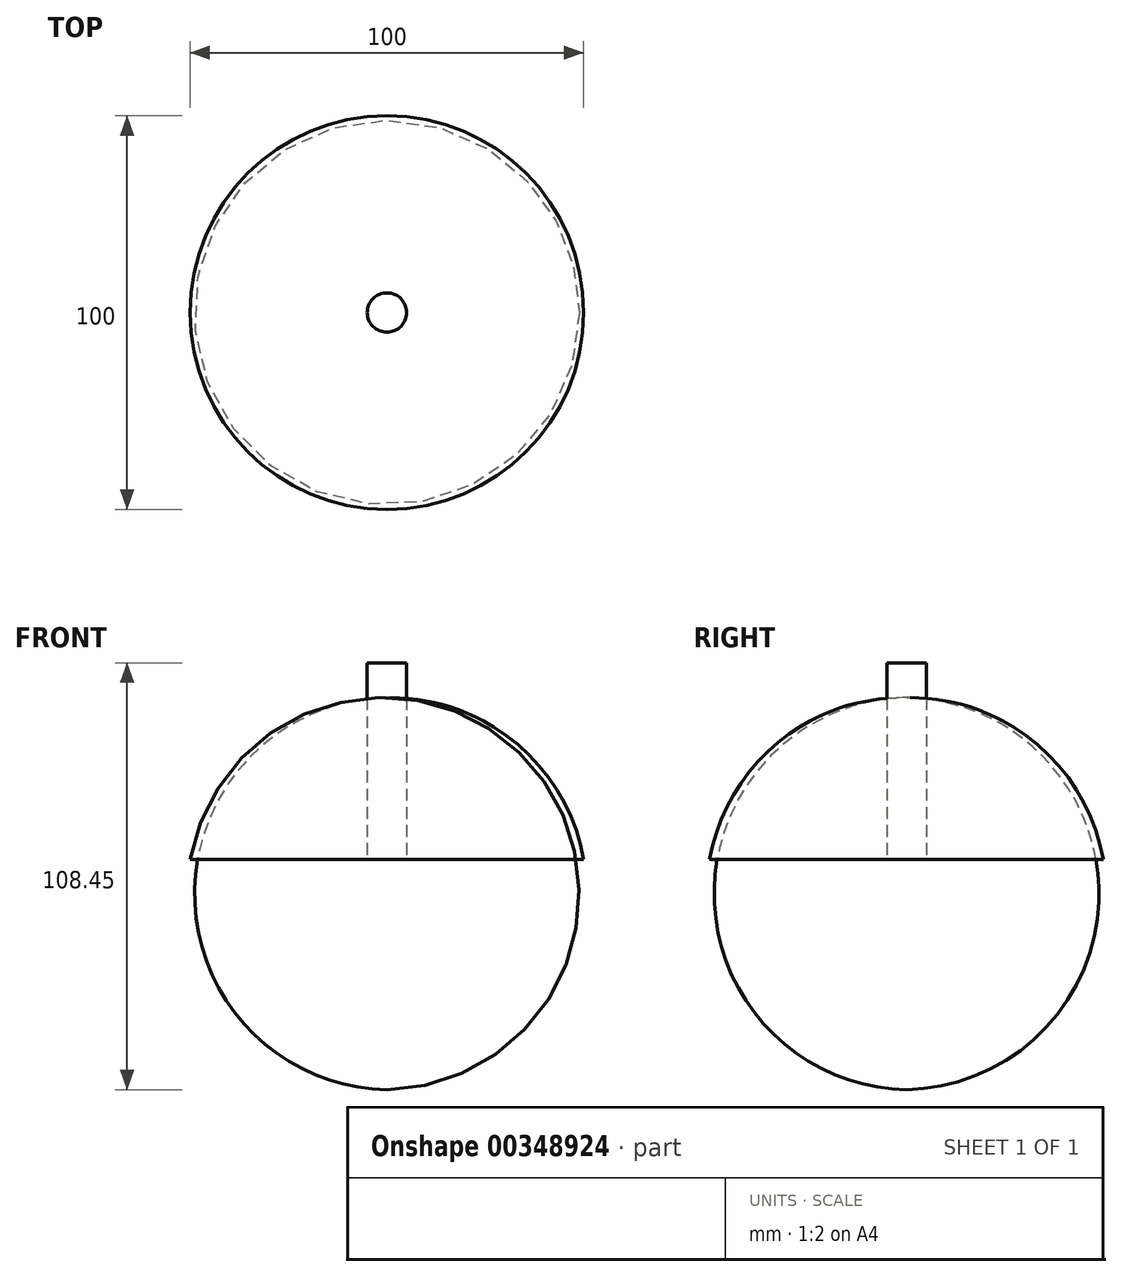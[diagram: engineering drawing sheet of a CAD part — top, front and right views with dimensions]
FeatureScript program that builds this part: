
annotation { "Feature Type Name" : "Feature", "Feature Type Description" : "" }
export const myFeature = defineFeature(function(context is Context, id is Id, definition is map)
    precondition{}
    {
        {
            var Q0;
            Q0=qCreatedBy(makeId("Front.planeOp"),FACE);
            var sketch = newSketch(context, id + "F0", { "sketchPlane" : qUnion([Q0])});
            skLineSegment(sketch, "E0.bottom", {"start": v(0, 0) * mm, "end": v(50, 0) * mm});
            skLineSegment(sketch, "E0.left", {"start": v(0, 0) * mm, "end": v(0, 41.15) * mm});
            skArc(sketch, "E1", {"start": v(50, 0) * mm, "mid": v(32.6, 29.8) * mm, "end": v(0, 41.15) * mm});
            skPoint(sketch, "E2.middle", {"position": v(16.59, 14.67) * mm});
            skLineSegment(sketch, "E3", {"start": v(19.13, 14.3) * mm, "end": v(19.4, 14.66) * mm, "construction": true});
            skLineSegment(sketch, "E4", {"start": v(16.59, 12.1) * mm, "end": v(16.62, 12.08) * mm, "construction": true});
            skFitSpline(sketch, "E5", {"points": [v(16.51, 16.92) * mm, v(20.39, 20.55) * mm, v(24.88, 22) * mm, v(22.66, 17.82) * mm], "startDerivative": vector(9.16, 11.04) * mm, "endDerivative": vector(-23.26, -14.59) * mm});
            skFitSpline(sketch, "E6", {"points": [v(22.66, 17.82) * mm, v(19.4, 14.66) * mm, v(18.83, 14.43) * mm, v(18.83, 14.4) * mm], "startDerivative": vector(-3.06, -8.88) * mm, "endDerivative": vector(0.1, -0.53) * mm});
            skFitSpline(sketch, "E7", {"points": [v(18.83, 14.4) * mm, v(21.75, 12.97) * mm, v(23.56, 10.14) * mm, v(24.88, 8.11) * mm], "startDerivative": vector(9.23, -3) * mm, "endDerivative": vector(4.43, -6.23) * mm});
            skFitSpline(sketch, "E8", {"points": [v(24.88, 8.11) * mm, v(25.94, 7.28) * mm, v(26.09, 7) * mm, v(25.28, 6.88) * mm, v(23.87, 7.33) * mm], "startDerivative": vector(4.07, -3.09) * mm, "endDerivative": vector(-4.32, 2) * mm});
            skFitSpline(sketch, "E9", {"points": [v(16.62, 12.08) * mm, v(18.93, 9.84) * mm, v(23.87, 7.33) * mm], "startDerivative": vector(4.6, -5.37) * mm, "endDerivative": vector(9.67, -4.2) * mm});
            skLineSegment(sketch, "E10.trimOffspring", {"start": v(18.83, 14.4) * mm, "end": v(18.83, 14.4) * mm});
            skPoint(sketch, "E11.orphan", {"position": v(24.88, 7.33) * mm});
            skFitSpline(sketch, "E12.MirrorCS", {"points": [v(16.66, 16.92) * mm, v(12.78, 20.55) * mm, v(8.3, 22) * mm, v(10.52, 17.82) * mm], "startDerivative": vector(-9.16, 11.04) * mm, "endDerivative": vector(23.26, -14.59) * mm});
            skFitSpline(sketch, "E13.MirrorCS", {"points": [v(10.52, 17.82) * mm, v(13.77, 14.66) * mm, v(14.34, 14.43) * mm, v(14.34, 14.4) * mm], "startDerivative": vector(3.06, -8.88) * mm, "endDerivative": vector(-0.1, -0.53) * mm});
            skFitSpline(sketch, "E14.MirrorCS", {"points": [v(14.34, 14.4) * mm, v(11.42, 12.97) * mm, v(9.61, 10.14) * mm, v(8.3, 8.11) * mm], "startDerivative": vector(-9.23, -3) * mm, "endDerivative": vector(-4.43, -6.23) * mm});
            skFitSpline(sketch, "E15.MirrorCS", {"points": [v(16.55, 12.08) * mm, v(14.25, 9.84) * mm, v(9.3, 7.33) * mm], "startDerivative": vector(-4.6, -5.37) * mm, "endDerivative": vector(-9.67, -4.2) * mm});
            skFitSpline(sketch, "E16.MirrorCS", {"points": [v(8.3, 8.11) * mm, v(7.23, 7.28) * mm, v(7.1, 7.06) * mm, v(7.9, 6.88) * mm, v(9.3, 7.33) * mm], "startDerivative": vector(-4.07, -3.09) * mm, "endDerivative": vector(4.32, 2) * mm});
            skPoint(sketch, "E17.orphan", {"position": v(16.59, 22) * mm});
            skPoint(sketch, "E18.orphan", {"position": v(8.3, 7.33) * mm});
            skLineSegment(sketch, "E19.trimOffspring", {"start": v(16.59, 7.33) * mm, "end": v(16.59, 7.01) * mm, "construction": true});
            skEllipse(sketch, "E20", {"center": v(32.68, 12.4) * mm, "majorRadius": 2.06 * mm, "minorRadius": 0.68 * mm, "majorAxis": v(0.9, -0.43)});
            skFitSpline(sketch, "E21", {"points": [v(6.55, 37.72) * mm, v(6.85, 34.97) * mm, v(10.86, 33.56) * mm, v(12.41, 32.82) * mm, v(11.08, 35.57) * mm, v(8.48, 36.46) * mm, v(6.55, 37.72) * mm]});
            skFitSpline(sketch, "E22", {"points": [v(20.8, 27.7) * mm, v(21.47, 30) * mm, v(25.25, 31.4) * mm, v(25.85, 33.34) * mm, v(26.89, 29.33) * mm, v(23.92, 27.85) * mm, v(22.21, 26.07) * mm, v(20.8, 26.14) * mm, v(20.8, 27.7) * mm]});
            skFitSpline(sketch, "E23", {"points": [v(34.53, 8.55) * mm, v(34.75, 6.03) * mm, v(37.35, 5.43) * mm, v(38.4, 2.98) * mm, v(39.2, 5.58) * mm, v(38.84, 7.14) * mm, v(37.28, 7.51) * mm, v(35.42, 11.15) * mm, v(34.53, 8.55) * mm]});
            skFitSpline(sketch, "E24", {"points": [v(29.56, 20.5) * mm, v(31.2, 22.73) * mm, v(34.53, 23.91) * mm, v(34.6, 25.1) * mm, v(36.02, 21.9) * mm, v(34.46, 19.76) * mm, v(31.79, 18.72) * mm, v(28.97, 15.45) * mm, v(29.26, 19.68) * mm, v(29.56, 20.5) * mm]});
            skFitSpline(sketch, "E25", {"points": [v(4.7, 16.34) * mm, v(2.4, 15.3) * mm, v(1.73, 12.78) * mm, v(2.62, 9.59) * mm, v(3.43, 11) * mm, v(4.47, 13.15) * mm, v(6.77, 13.6) * mm, v(7.37, 15.45) * mm, v(8.3, 16.27) * mm, v(8.3, 17.46) * mm, v(4.7, 16.34) * mm]});
            skFitSpline(sketch, "E26", {"points": [v(7, 30.22) * mm, v(7.81, 28.14) * mm, v(11.67, 26.73) * mm, v(12.12, 25.1) * mm, v(13.23, 27.03) * mm, v(12.71, 28.44) * mm, v(10.41, 29.33) * mm, v(9.07, 29.33) * mm, v(7, 30.22) * mm]});
            skLineSegment(sketch, "E27", {"start": v(-53.14, 0) * mm, "end": v(62.64, 0) * mm, "construction": true});
            skLineSegment(sketch, "E28", {"start": v(0, 59.9) * mm, "end": v(0, -67.76) * mm, "construction": true});
            skLineSegment(sketch, "E29.trimOffspring", {"start": v(10.41, 29.33) * mm, "end": v(10.3, 29.33) * mm, "construction": true});
            skPoint(sketch, "E30.start.orphan", {"position": v(33.17, 29.33) * mm});
            skSolve(sketch);
        }
        {
            var Q0;
            Q0=makeQuery(id+"F0.imprint","IMPRINT",FACE,{"disambiguationData":[TD([[makeQuery(id+"F0.imprint","IMPRINT",EDGE,{"derivedFrom":sQuery(id+"F0.wireOp",EDGE,"E26")}),1.0]])]});
            var Q1;
            Q1=makeQuery(id+"F0.imprint","IMPRINT",FACE,{"disambiguationData":[TD([[makeQuery(id+"F0.imprint","IMPRINT",EDGE,{"derivedFrom":sQuery(id+"F0.wireOp",EDGE,"E21")}),1.0]])]});
            var Q2;
            Q2=makeQuery(id+"F0.imprint","IMPRINT",FACE,{"disambiguationData":[TD([[makeQuery(id+"F0.imprint","IMPRINT",EDGE,{"derivedFrom":sQuery(id+"F0.wireOp",EDGE,"E20")}),1.0]])]});
            var Q3;
            Q3=makeQuery(id+"F0.imprint","IMPRINT",FACE,{"disambiguationData":[TD([[makeQuery(id+"F0.imprint","IMPRINT",EDGE,{"derivedFrom":sQuery(id+"F0.wireOp",EDGE,"E23")}),1.0]])]});
            var Q4;
            Q4=makeQuery(id+"F0.imprint","IMPRINT",FACE,{"disambiguationData":[TD([[makeQuery(id+"F0.imprint","IMPRINT",EDGE,{"derivedFrom":sQuery(id+"F0.wireOp",EDGE,"E22")}),-1.0]])]});
            var Q5;
            Q5=makeQuery(id+"F0.imprint","IMPRINT",FACE,{"disambiguationData":[TD([[makeQuery(id+"F0.imprint","IMPRINT",EDGE,{"derivedFrom":sQuery(id+"F0.wireOp",EDGE,"E0.bottom")}),1.0]])]});
            var Q6;
            Q6=makeQuery(id+"F0.imprint","IMPRINT",FACE,{"disambiguationData":[TD([[makeQuery(id+"F0.imprint","IMPRINT",EDGE,{"derivedFrom":sQuery(id+"F0.wireOp",EDGE,"E24")}),-1.0]])]});
            var Q7;
            Q7=makeQuery(id+"F0.imprint","IMPRINT",FACE,{"disambiguationData":[TD([[makeQuery(id+"F0.imprint","IMPRINT",EDGE,{"derivedFrom":sQuery(id+"F0.wireOp",EDGE,"E25")}),1.0]])]});
            var Q8;
            Q8=sQuery(id+"F0.wireOp",EDGE,"E0.left");
            revolve(context, id + "F1", {"entities" : qUnion([Q0, Q1, Q2, Q3, Q4, Q5, Q6, Q7]), "axis" : qUnion([Q8]), "revolveType" : RevolveType.FULL});
        }
        {
            var Q0;
            Q0=qCreatedBy(makeId("Top.planeOp"),FACE);
            var sketch = newSketch(context, id + "F2", { "sketchPlane" : qUnion([Q0])});
            skCircle(sketch, "E31", {"center": v(0, 0) * mm, "radius": 5 * mm});
            skSolve(sketch);
        }
        {
            var Q0;
            Q0=makeQuery(id+"F2.imprint","IMPRINT",FACE,{"disambiguationData":[TD([[makeQuery(id+"F2.imprint","IMPRINT",EDGE,{"derivedFrom":sQuery(id+"F2.wireOp",EDGE,"E31")}),1.0]])]});
            extrude(context, id + "F3", {"entities" : qUnion([Q0]), "depth" : 50 * mm});
        }
    });
